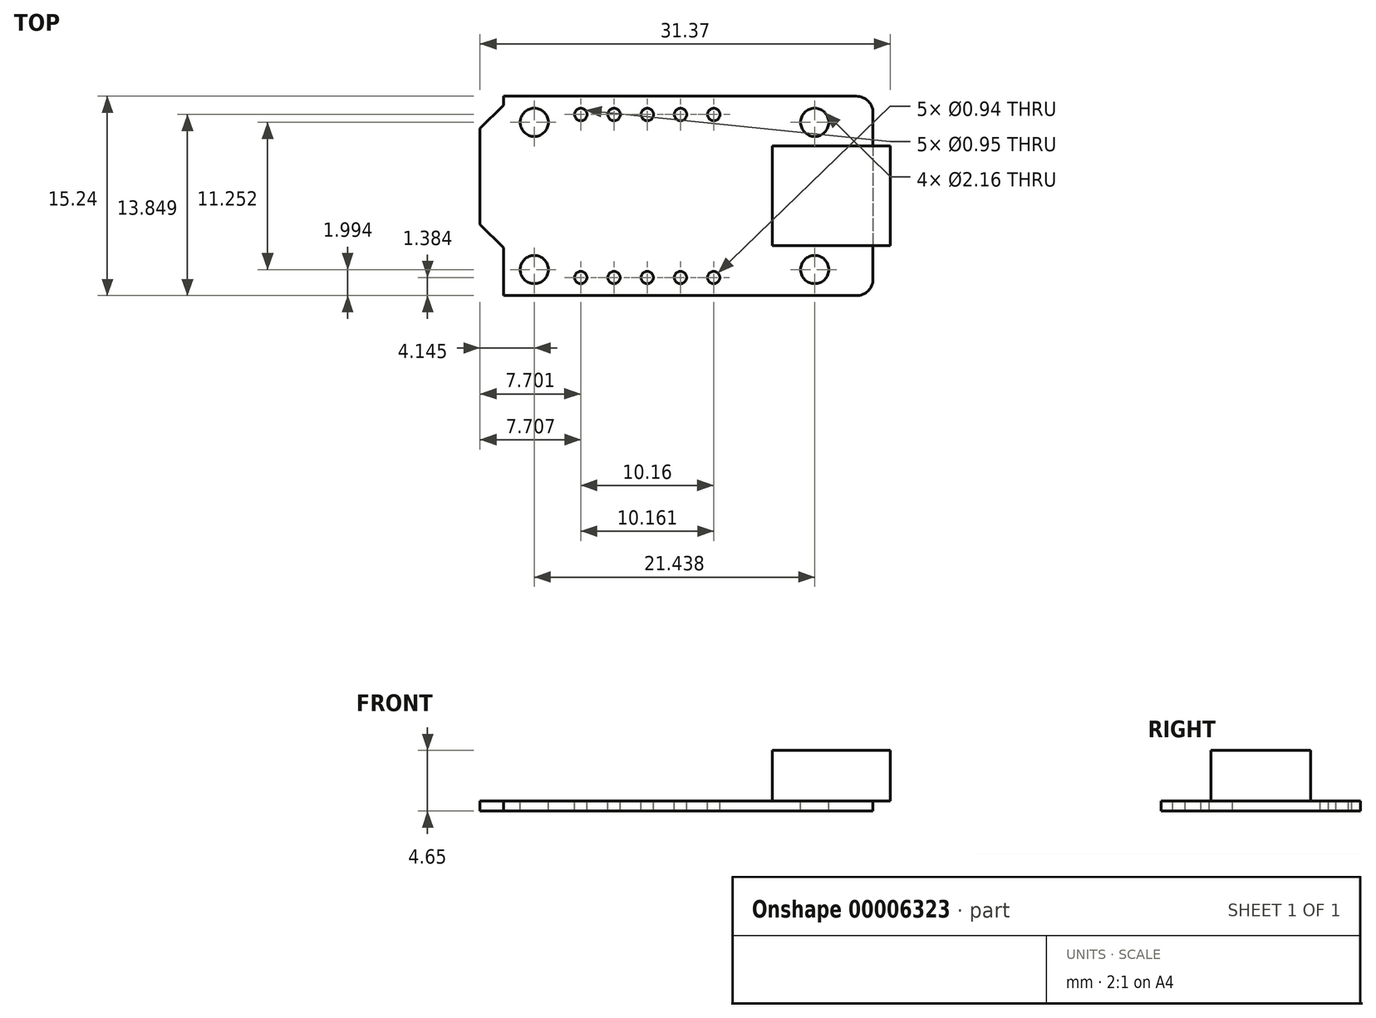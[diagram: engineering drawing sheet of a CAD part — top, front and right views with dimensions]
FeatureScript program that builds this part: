
annotation { "Feature Type Name" : "Feature", "Feature Type Description" : "" }
export const myFeature = defineFeature(function(context is Context, id is Id, definition is map)
    precondition{}
    {
        {
            var Q0;
            Q0=qCreatedBy(makeId("Top.planeOp"),FACE);
            var sketch = newSketch(context, id + "F0", { "sketchPlane" : qUnion([Q0])});
            skLineSegment(sketch, "E0.bottom", {"start": v(-1.27, 0) * mm, "end": v(-28.24, 0) * mm});
            skLineSegment(sketch, "E0.top", {"start": v(-1.27, -15.24) * mm, "end": v(-28.24, -15.24) * mm});
            skLineSegment(sketch, "E0.left", {"start": v(0, -1.27) * mm, "end": v(0, -13.97) * mm});
            skLineSegment(sketch, "E0.right", {"start": v(-28.24, 0) * mm, "end": v(-28.24, -0.68) * mm});
            skLineSegment(sketch, "E1", {"start": v(-28.24, -0.68) * mm, "end": v(-30.04, -2.47) * mm});
            skLineSegment(sketch, "E2", {"start": v(-30.04, -2.47) * mm, "end": v(-30.04, -9.79) * mm});
            skLineSegment(sketch, "E3", {"start": v(-30.04, -9.79) * mm, "end": v(-28.24, -11.58) * mm});
            skLineSegment(sketch, "E4.trimOffspring", {"start": v(-28.24, -11.58) * mm, "end": v(-28.24, -15.24) * mm});
            skPoint(sketch, "E5.visualSharp", {"position": v(0, 0) * mm});
            skArc(sketch, "E5.filletArc", {"start": v(0, -1.27) * mm, "mid": v(-0.37, -0.37) * mm, "end": v(-1.27, 0) * mm});
            skPoint(sketch, "E6.visualSharp", {"position": v(0, -15.24) * mm});
            skArc(sketch, "E6.filletArc", {"start": v(-1.27, -15.24) * mm, "mid": v(-0.37, -14.87) * mm, "end": v(0, -13.97) * mm});
            skSolve(sketch);
        }
        {
            var Q0;
            Q0 = qSketchRegion(id + "F0", true);
            var Q1;
            Q1 = qSketchRegion(id + "F2", true);
            extrude(context, id + "F1", {"entities" : qUnion([Q0, Q1]), "depth" : 0.79 * mm});
        }
        {
            var Q0;
            Q0=makeQuery(id+"F1.opExtrude","CAP_FACE",FACE,{"disambiguationData":[OSD([sQuery(id+"F0.wireOp",EDGE,"E0.bottom"),sQuery(id+"F0.wireOp",EDGE,"E0.top"),sQuery(id+"F0.wireOp",EDGE,"E0.left"),sQuery(id+"F0.wireOp",EDGE,"E0.right"),sQuery(id+"F0.wireOp",EDGE,"E1"),sQuery(id+"F0.wireOp",EDGE,"E2"),sQuery(id+"F0.wireOp",EDGE,"E3"),sQuery(id+"F0.wireOp",EDGE,"E4.trimOffspring"),sQuery(id+"F0.wireOp",EDGE,"E5.filletArc"),sQuery(id+"F0.wireOp",EDGE,"E6.filletArc")])],"isStart":false});
            var sketch = newSketch(context, id + "F2", { "sketchPlane" : qUnion([Q0])});
            skCircle(sketch, "E7", {"center": v(-25.9, -13.25) * mm, "radius": 1.08 * mm});
            skCircle(sketch, "E8", {"center": v(-25.9, -2) * mm, "radius": 1.08 * mm});
            skCircle(sketch, "E9", {"center": v(-4.46, -2) * mm, "radius": 1.08 * mm});
            skCircle(sketch, "E10", {"center": v(-4.46, -13.25) * mm, "radius": 1.08 * mm});
            skCircle(sketch, "E11", {"center": v(-22.33, -1.4) * mm, "radius": 0.48 * mm});
            skCircle(sketch, "E12.1.0.0", {"center": v(-19.8, -1.4) * mm, "radius": 0.48 * mm});
            skCircle(sketch, "E12.2.0.0", {"center": v(-17.25, -1.4) * mm, "radius": 0.48 * mm});
            skCircle(sketch, "E12.3.0.0", {"center": v(-14.71, -1.4) * mm, "radius": 0.48 * mm});
            skCircle(sketch, "E12.4.0.0", {"center": v(-12.17, -1.4) * mm, "radius": 0.48 * mm});
            skLineSegment(sketch, "E12.direction1", {"start": v(-22.33, -1.4) * mm, "end": v(-19.8, -1.4) * mm, "construction": true});
            skCircle(sketch, "E13", {"center": v(-22.34, -13.86) * mm, "radius": 0.47 * mm});
            skCircle(sketch, "E14.1.0.0", {"center": v(-19.8, -13.86) * mm, "radius": 0.47 * mm});
            skCircle(sketch, "E14.2.0.0", {"center": v(-17.26, -13.86) * mm, "radius": 0.47 * mm});
            skCircle(sketch, "E14.3.0.0", {"center": v(-14.72, -13.86) * mm, "radius": 0.47 * mm});
            skCircle(sketch, "E14.4.0.0", {"center": v(-12.18, -13.86) * mm, "radius": 0.47 * mm});
            skLineSegment(sketch, "E14.direction1", {"start": v(-22.34, -13.86) * mm, "end": v(-19.8, -13.86) * mm, "construction": true});
            skSolve(sketch);
        }
        {
            var Q0;
            Q0 = qSketchRegion(id + "F2", true);
            extrude(context, id + "F3", {"entities" : qUnion([Q0]), "operationType" : NewBodyOperationType.REMOVE, "endBound" : BoundingType.THROUGH_ALL, "oppositeDirection" : true, "depth" : 25.4 * mm});
        }
        {
            var Q0;
            Q0=makeQuery(id+"F1.opExtrude","CAP_FACE",FACE,{"disambiguationData":[OSD([sQuery(id+"F0.wireOp",EDGE,"E0.bottom"),sQuery(id+"F0.wireOp",EDGE,"E0.top"),sQuery(id+"F0.wireOp",EDGE,"E0.left"),sQuery(id+"F0.wireOp",EDGE,"E0.right"),sQuery(id+"F0.wireOp",EDGE,"E1"),sQuery(id+"F0.wireOp",EDGE,"E2"),sQuery(id+"F0.wireOp",EDGE,"E3"),sQuery(id+"F0.wireOp",EDGE,"E4.trimOffspring"),sQuery(id+"F0.wireOp",EDGE,"E5.filletArc"),sQuery(id+"F0.wireOp",EDGE,"E6.filletArc")])],"isStart":false});
            var sketch = newSketch(context, id + "F4", { "sketchPlane" : qUnion([Q0])});
            skLineSegment(sketch, "E15.bottom", {"start": v(1.33, -3.81) * mm, "end": v(-7.7, -3.81) * mm});
            skLineSegment(sketch, "E15.top", {"start": v(1.33, -11.43) * mm, "end": v(-7.7, -11.43) * mm});
            skLineSegment(sketch, "E15.left", {"start": v(1.33, -3.8) * mm, "end": v(1.33, -11.43) * mm});
            skLineSegment(sketch, "E15.right", {"start": v(-7.7, -3.81) * mm, "end": v(-7.7, -11.43) * mm});
            skPoint(sketch, "E16", {"position": v(0, -7.62) * mm});
            skLineSegment(sketch, "E17", {"start": v(0, -7.62) * mm, "end": v(-17.46, -7.62) * mm, "construction": true});
            skPoint(sketch, "E18", {"position": v(-7.7, -7.62) * mm});
            skSolve(sketch);
        }
        {
            var Q0;
            Q0 = qSketchRegion(id + "F4", true);
            extrude(context, id + "F5", {"entities" : qUnion([Q0]), "operationType" : NewBodyOperationType.ADD, "depth" : 3.86 * mm});
        }
    });
